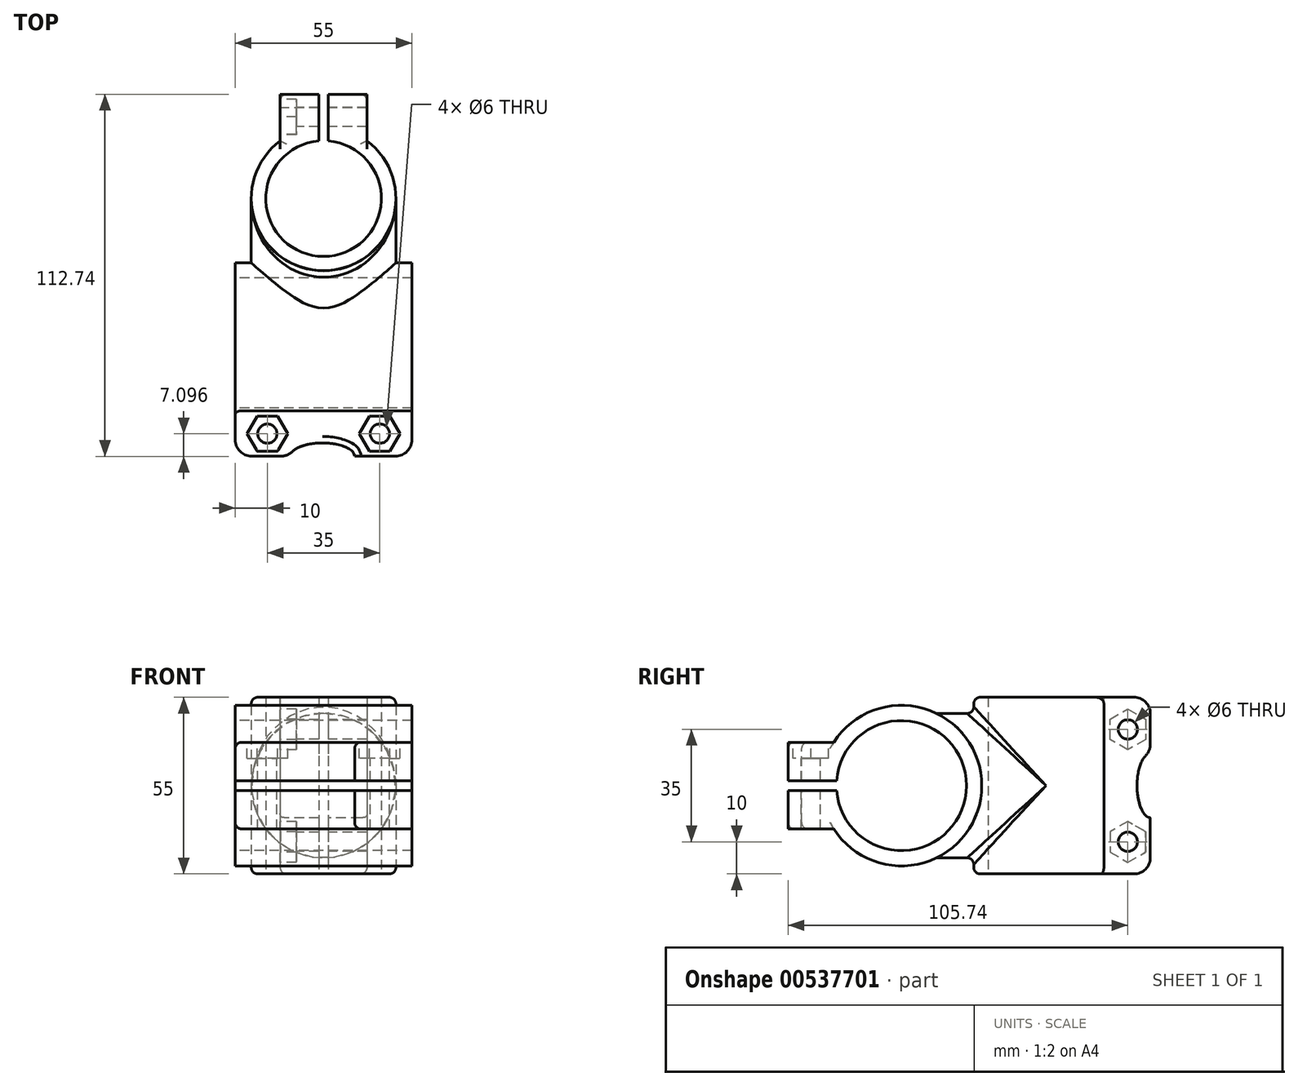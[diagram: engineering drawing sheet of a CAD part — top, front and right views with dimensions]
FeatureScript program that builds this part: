
annotation { "Feature Type Name" : "Feature", "Feature Type Description" : "" }
export const myFeature = defineFeature(function(context is Context, id is Id, definition is map)
    precondition{}
    {
        {
            var Q0;
            Q0=qCreatedBy(makeId("Top.planeOp"),FACE);
            var sketch = newSketch(context, id + "F0", { "sketchPlane" : qUnion([Q0])});
            skArc(sketch, "E0", {"start": v(-1.5, 17.94) * mm, "mid": v(0, -18) * mm, "end": v(1.5, 17.94) * mm});
            skArc(sketch, "E1", {"start": v(-13.5, 18) * mm, "mid": v(0, -22.5) * mm, "end": v(13.5, 18) * mm});
            skLineSegment(sketch, "E2", {"start": v(-1.5, 17.94) * mm, "end": v(-1.5, 22.45) * mm});
            skLineSegment(sketch, "E3", {"start": v(1.5, 17.94) * mm, "end": v(1.5, 22.45) * mm});
            skLineSegment(sketch, "E4", {"start": v(1.5, 20.2) * mm, "end": v(1.5, 22.45) * mm});
            skPoint(sketch, "E4.endSnap0", {"position": v(1.5, 20.2) * mm});
            skLineSegment(sketch, "E5", {"start": v(-1.5, 17.94) * mm, "end": v(-1.5, 32.45) * mm});
            skPoint(sketch, "E5.endSnap0", {"position": v(-1.5, 20.2) * mm});
            skPoint(sketch, "E6.orphan", {"position": v(1.5, 29.76) * mm});
            skLineSegment(sketch, "E7", {"start": v(1.5, 17.94) * mm, "end": v(1.5, 32.45) * mm});
            skLineSegment(sketch, "E8", {"start": v(-13.5, 18) * mm, "end": v(-13.5, 32.45) * mm});
            skLineSegment(sketch, "E9", {"start": v(13.5, 18) * mm, "end": v(13.5, 32.45) * mm});
            skLineSegment(sketch, "E10", {"start": v(-13.5, 32.45) * mm, "end": v(-1.5, 32.45) * mm});
            skLineSegment(sketch, "E11", {"start": v(1.5, 32.45) * mm, "end": v(13.5, 32.45) * mm});
            skSolve(sketch);
        }
        {
            var Q0;
            {var subQ1=sQuery(id+"F0.wireOp",EDGE,"E0");Q0=makeQuery(id+"F0.imprint","IMPRINT",FACE,{"disambiguationData":[TD([[makeQuery(id+"F0.imprint","IMPRINT",EDGE,{"derivedFrom":subQ1}),-1.0]])]});}
            extrude(context, id + "F1", {"entities" : qUnion([Q0]), "depth" : 55 * mm, "offsetDistance" : 25.4 * mm});
        }
        {
            var Q0;
            Q0=qCreatedBy(makeId("Front.planeOp"),FACE);
            var sketch = newSketch(context, id + "F2", { "sketchPlane" : qUnion([Q0])});
            skCircle(sketch, "E12", {"center": v(0, 27.5) * mm, "radius": 22.5 * mm});
            skSolve(sketch);
        }
        {
            var Q0;
            Q0=makeQuery(id+"F2.imprint","IMPRINT",FACE,{"disambiguationData":[TD([[makeQuery(id+"F2.imprint","IMPRINT",EDGE,{"derivedFrom":sQuery(id+"F2.wireOp",EDGE,"E12")}),1.0]])]});
            extrude(context, id + "F3", {"entities" : qUnion([Q0]), "operationType" : NewBodyOperationType.ADD, "depth" : 45 * mm, "offsetDistance" : 25.4 * mm});
        }
        {
            var Q0;
            Q0=makeQuery(id+"F1.opExtrude","CAP_FACE",FACE,{"disambiguationData":[OSD([sQuery(id+"F0.wireOp",EDGE,"E0"),sQuery(id+"F0.wireOp",EDGE,"E1"),sQuery(id+"F0.wireOp",EDGE,"E5"),sQuery(id+"F0.wireOp",EDGE,"E7"),sQuery(id+"F0.wireOp",EDGE,"E8"),sQuery(id+"F0.wireOp",EDGE,"E9"),sQuery(id+"F0.wireOp",EDGE,"E10"),sQuery(id+"F0.wireOp",EDGE,"E11")])],"isStart":true});
            var sketch = newSketch(context, id + "F4", { "sketchPlane" : qUnion([Q0])});
            skPoint(sketch, "E13", {"position": v(0, 0) * mm});
            skCircle(sketch, "E14", {"center": v(0, 0) * mm, "radius": 18 * mm});
            skSolve(sketch);
        }
        {
            var Q0;
            Q0=sQuery(id+"F4.wireOp",VERTEX,"E13");
            var Q1;
            Q1=makeQuery(id+"F1.opExtrude","SWEPT_BODY",BODY,{"disambiguationData":[OSD([sQuery(id+"F0.wireOp",EDGE,"E0"),sQuery(id+"F0.wireOp",EDGE,"E1"),sQuery(id+"F0.wireOp",EDGE,"E5"),sQuery(id+"F0.wireOp",EDGE,"E7"),sQuery(id+"F0.wireOp",EDGE,"E8"),sQuery(id+"F0.wireOp",EDGE,"E9"),sQuery(id+"F0.wireOp",EDGE,"E10"),sQuery(id+"F0.wireOp",EDGE,"E11")])]});
            hole(context, id + "F5", {"style" : HoleStyle.SIMPLE, "endStyle" : HoleEndStyle.THROUGH, "holeDiameter" : 36 * mm, "isTappedThrough" : true, "tappedDepth" : 12.7 * mm, "tapClearance" : 3, "startFromSketch" : true, "locations" : qUnion([Q0]), "scope" : qUnion([Q1])});
        }
        {
            var Q0;
            Q0=qCreatedBy(makeId("Right.planeOp"),FACE);
            var sketch = newSketch(context, id + "F6", { "sketchPlane" : qUnion([Q0])});
            skArc(sketch, "E15", {"start": v(-65.2, 26) * mm, "mid": v(-24.75, 27.5) * mm, "end": v(-65.2, 29) * mm});
            skArc(sketch, "E16", {"start": v(-66.04, 14) * mm, "mid": v(-20, 27.5) * mm, "end": v(-66.04, 41) * mm});
            skLineSegment(sketch, "E17", {"start": v(-45, 27.5) * mm, "end": v(-45.7, 27.5) * mm});
            skLineSegment(sketch, "E18", {"start": v(-65.2, 26) * mm, "end": v(-80.2, 26) * mm});
            skLineSegment(sketch, "E19", {"start": v(-65.2, 29) * mm, "end": v(-80.2, 29) * mm});
            skLineSegment(sketch, "E20", {"start": v(-66.04, 14) * mm, "end": v(-80.2, 14) * mm});
            skLineSegment(sketch, "E21", {"start": v(-80.2, 26) * mm, "end": v(-80.2, 14) * mm});
            skLineSegment(sketch, "E22.MirrorCS", {"start": v(-80.2, 29) * mm, "end": v(-80.2, 41) * mm});
            skLineSegment(sketch, "E23.MirrorCS", {"start": v(-66.04, 41) * mm, "end": v(-80.2, 41) * mm});
            skArc(sketch, "E24.MirrorC", {"start": v(-66.04, 41) * mm, "mid": v(-20, 27.5) * mm, "end": v(-66.04, 14) * mm});
            skArc(sketch, "E25.MirrorC", {"start": v(-65.2, 29) * mm, "mid": v(-24.75, 27.5) * mm, "end": v(-65.2, 26) * mm});
            skPoint(sketch, "E26.orphan", {"position": v(-60.1, 14) * mm});
            skPoint(sketch, "E27.orphan", {"position": v(-60.1, 41) * mm});
            skPoint(sketch, "E28", {"position": v(-45, 68.44) * mm});
            skSolve(sketch);
        }
        {
            var Q0;
            Q0 = qSketchRegion(id + "F6", true);
            extrude(context, id + "F7", {"entities" : qUnion([Q0]), "operationType" : NewBodyOperationType.ADD, "endBound" : BoundingType.SYMMETRIC, "depth" : 55 * mm, "offsetDistance" : 25.4 * mm});
        }
        {
            var Q0;
            Q0=makeQuery(id+"F7.opExtrude","CAP_FACE",FACE,{"disambiguationData":[OSD([sQuery(id+"F6.wireOp",EDGE,"E18"),sQuery(id+"F6.wireOp",EDGE,"E20"),sQuery(id+"F6.wireOp",EDGE,"E21"),sQuery(id+"F6.wireOp",EDGE,"E22.MirrorCS"),sQuery(id+"F6.wireOp",EDGE,"E23.MirrorCS"),sQuery(id+"F6.wireOp",EDGE,"E24.MirrorC"),sQuery(id+"F6.wireOp",EDGE,"E19"),sQuery(id+"F6.wireOp",EDGE,"E25.MirrorC")])],"isStart":false});
            var sketch = newSketch(context, id + "F8", { "sketchPlane" : qUnion([Q0])});
            skPoint(sketch, "E29", {"position": v(-45, 27.5) * mm});
            skSolve(sketch);
        }
        {
            var Q0;
            Q0=sQuery(id+"F8.wireOp",VERTEX,"E29");
            var Q1;
            Q1=makeQuery(id+"F1.opExtrude","SWEPT_BODY",BODY,{"disambiguationData":[OSD([sQuery(id+"F0.wireOp",EDGE,"E0"),sQuery(id+"F0.wireOp",EDGE,"E1"),sQuery(id+"F0.wireOp",EDGE,"E5"),sQuery(id+"F0.wireOp",EDGE,"E7"),sQuery(id+"F0.wireOp",EDGE,"E8"),sQuery(id+"F0.wireOp",EDGE,"E9"),sQuery(id+"F0.wireOp",EDGE,"E10"),sQuery(id+"F0.wireOp",EDGE,"E11")])]});
            hole(context, id + "F9", {"style" : HoleStyle.SIMPLE, "endStyle" : HoleEndStyle.THROUGH, "holeDiameter" : 40.5 * mm, "isTappedThrough" : true, "tappedDepth" : 12.7 * mm, "tapClearance" : 3, "startFromSketch" : true, "locations" : qUnion([Q0]), "scope" : qUnion([Q1])});
        }
        {
            var Q0;
            Q0=makeQuery(id+"F1.opExtrude","SWEPT_FACE",FACE,{"disambiguationData":[OSD([sQuery(id+"F0.wireOp",EDGE,"E8")])]});
            var sketch = newSketch(context, id + "F10", { "sketchPlane" : qUnion([Q0])});
            skCircle(sketch, "E30.cCircle", {"center": v(-25.45, 10) * mm, "radius": 5.5 * mm, "construction": true});
            skLineSegment(sketch, "E30.0", {"start": v(-25.46, 16.35) * mm, "end": v(-19.96, 13.19) * mm});
            skLineSegment(sketch, "E30.1", {"start": v(-19.96, 13.19) * mm, "end": v(-19.94, 6.83) * mm});
            skLineSegment(sketch, "E30.2", {"start": v(-19.94, 6.83) * mm, "end": v(-25.44, 3.65) * mm});
            skLineSegment(sketch, "E30.3", {"start": v(-25.44, 3.65) * mm, "end": v(-30.94, 6.81) * mm});
            skLineSegment(sketch, "E30.4", {"start": v(-30.94, 6.81) * mm, "end": v(-30.96, 13.17) * mm});
            skLineSegment(sketch, "E30.5", {"start": v(-30.96, 13.17) * mm, "end": v(-25.46, 16.35) * mm});
            skPoint(sketch, "E30.0.midPoint", {"position": v(-22.7, 14.77) * mm});
            skPoint(sketch, "E31.endSnap0", {"position": v(-32.45, 27.5) * mm});
            skPoint(sketch, "E31.start.orphan", {"position": v(0, 27.48) * mm});
            skLineSegment(sketch, "E32.MirrorCS", {"start": v(-30.94, 48.19) * mm, "end": v(-30.96, 41.83) * mm});
            skPoint(sketch, "E33.MirrorP", {"position": v(-25.45, 45) * mm});
            skLineSegment(sketch, "E34.MirrorCS", {"start": v(-19.94, 48.17) * mm, "end": v(-25.44, 51.35) * mm});
            skLineSegment(sketch, "E35.MirrorCS", {"start": v(-30.96, 41.83) * mm, "end": v(-25.46, 38.65) * mm});
            skLineSegment(sketch, "E36.MirrorCS", {"start": v(-25.46, 38.65) * mm, "end": v(-19.96, 41.81) * mm});
            skLineSegment(sketch, "E37.MirrorCS", {"start": v(-25.44, 51.35) * mm, "end": v(-30.94, 48.19) * mm});
            skPoint(sketch, "E38.MirrorP", {"position": v(-22.7, 40.23) * mm});
            skLineSegment(sketch, "E39.MirrorCS", {"start": v(-19.96, 41.81) * mm, "end": v(-19.94, 48.17) * mm});
            skCircle(sketch, "E40.MirrorC", {"center": v(-25.45, 45) * mm, "radius": 5.5 * mm, "construction": true});
            skSolve(sketch);
        }
        {
            var Q0;
            Q0 = qSketchRegion(id + "F10", true);
            extrude(context, id + "F11", {"entities" : qUnion([Q0]), "operationType" : NewBodyOperationType.REMOVE, "oppositeDirection" : true, "depth" : 5 * mm, "offsetDistance" : 25.4 * mm});
        }
        {
            var Q0;
            Q0=makeQuery(id+"F1.opExtrude","SWEPT_FACE",FACE,{"disambiguationData":[OSD([sQuery(id+"F0.wireOp",EDGE,"E8")])]});
            var sketch = newSketch(context, id + "F12", { "sketchPlane" : qUnion([Q0])});
            skPoint(sketch, "E41", {"position": v(-25.45, 10) * mm});
            skPoint(sketch, "E42.orphan", {"position": v(-19.96, 13.19) * mm});
            skPoint(sketch, "E43.start.orphan", {"position": v(-30.94, 6.81) * mm});
            skPoint(sketch, "E44.start.orphan", {"position": v(0, 27.52) * mm});
            skLineSegment(sketch, "E45", {"start": v(-38, 27.98) * mm, "end": v(-12.83, 27.98) * mm});
            skSolve(sketch);
        }
        {
            var Q0;
            Q0=sQuery(id+"F12.wireOp",VERTEX,"f4a95eb3-fcfc-4df5-b017-d8c500dd858f2.MirrorP");
            var Q1;
            Q1=sQuery(id+"F12.wireOp",VERTEX,"E41");
            var Q2;
            Q2=makeQuery(id+"F1.opExtrude","SWEPT_BODY",BODY,{"disambiguationData":[OSD([sQuery(id+"F0.wireOp",EDGE,"E0"),sQuery(id+"F0.wireOp",EDGE,"E1"),sQuery(id+"F0.wireOp",EDGE,"E5"),sQuery(id+"F0.wireOp",EDGE,"E7"),sQuery(id+"F0.wireOp",EDGE,"E8"),sQuery(id+"F0.wireOp",EDGE,"E9"),sQuery(id+"F0.wireOp",EDGE,"E10"),sQuery(id+"F0.wireOp",EDGE,"E11")])]});
            hole(context, id + "F13", {"style" : HoleStyle.SIMPLE, "endStyle" : HoleEndStyle.THROUGH, "holeDiameter" : 6 * mm, "isTappedThrough" : true, "tappedDepth" : 12.7 * mm, "tapClearance" : 3, "startFromSketch" : true, "locations" : qUnion([Q0, Q1]), "scope" : qUnion([Q2])});
        }
        {
            var Q0;
            Q0=makeQuery(id+"F7.opExtrude","SWEPT_FACE",FACE,{"disambiguationData":[OSD([sQuery(id+"F6.wireOp",EDGE,"E23.MirrorCS")])]});
            var sketch = newSketch(context, id + "F14", { "sketchPlane" : qUnion([Q0])});
            skCircle(sketch, "E46.cCircle", {"center": v(-17.5, -73.2) * mm, "radius": 5.5 * mm, "construction": true});
            skLineSegment(sketch, "E46.0", {"start": v(-11.15, -73.2) * mm, "end": v(-14.32, -78.7) * mm});
            skLineSegment(sketch, "E46.1", {"start": v(-14.32, -78.7) * mm, "end": v(-20.68, -78.7) * mm});
            skLineSegment(sketch, "E46.2", {"start": v(-20.68, -78.7) * mm, "end": v(-23.85, -73.2) * mm});
            skLineSegment(sketch, "E46.3", {"start": v(-23.85, -73.2) * mm, "end": v(-20.68, -67.7) * mm});
            skLineSegment(sketch, "E46.4", {"start": v(-20.68, -67.7) * mm, "end": v(-14.32, -67.7) * mm});
            skLineSegment(sketch, "E46.5", {"start": v(-14.32, -67.7) * mm, "end": v(-11.15, -73.2) * mm});
            skPoint(sketch, "E46.0.midPoint", {"position": v(-12.74, -75.94) * mm});
            skLineSegment(sketch, "E47.MirrorCS", {"start": v(11.15, -73.2) * mm, "end": v(14.32, -78.7) * mm});
            skCircle(sketch, "E48.MirrorC", {"center": v(17.5, -73.2) * mm, "radius": 5.5 * mm, "construction": true});
            skPoint(sketch, "E49.MirrorP", {"position": v(12.74, -75.94) * mm});
            skLineSegment(sketch, "E50.MirrorCS", {"start": v(14.32, -78.7) * mm, "end": v(20.68, -78.7) * mm});
            skLineSegment(sketch, "E51.MirrorCS", {"start": v(20.68, -67.7) * mm, "end": v(14.32, -67.7) * mm});
            skLineSegment(sketch, "E52.MirrorCS", {"start": v(14.32, -67.7) * mm, "end": v(11.15, -73.2) * mm});
            skLineSegment(sketch, "E53.MirrorCS", {"start": v(23.85, -73.2) * mm, "end": v(20.68, -67.7) * mm});
            skLineSegment(sketch, "E54.MirrorCS", {"start": v(20.68, -78.7) * mm, "end": v(23.85, -73.2) * mm});
            skSolve(sketch);
        }
        {
            var Q0;
            Q0=sQuery(id+"F14.wireOp",VERTEX,"E46.cCircle.center");
            var Q1;
            Q1=sQuery(id+"F14.wireOp",VERTEX,"E48.MirrorC.center");
            var Q2;
            Q2=makeQuery(id+"F1.opExtrude","SWEPT_BODY",BODY,{"disambiguationData":[OSD([sQuery(id+"F0.wireOp",EDGE,"E0"),sQuery(id+"F0.wireOp",EDGE,"E1"),sQuery(id+"F0.wireOp",EDGE,"E5"),sQuery(id+"F0.wireOp",EDGE,"E7"),sQuery(id+"F0.wireOp",EDGE,"E8"),sQuery(id+"F0.wireOp",EDGE,"E9"),sQuery(id+"F0.wireOp",EDGE,"E10"),sQuery(id+"F0.wireOp",EDGE,"E11")])]});
            hole(context, id + "F15", {"style" : HoleStyle.SIMPLE, "endStyle" : HoleEndStyle.THROUGH, "holeDiameter" : 6 * mm, "isTappedThrough" : true, "tappedDepth" : 12.7 * mm, "tapClearance" : 3, "startFromSketch" : true, "locations" : qUnion([Q0, Q1]), "scope" : qUnion([Q2])});
        }
        {
            var Q0;
            Q0 = qSketchRegion(id + "F14", true);
            extrude(context, id + "F16", {"entities" : qUnion([Q0]), "operationType" : NewBodyOperationType.REMOVE, "oppositeDirection" : true, "depth" : 5 * mm, "offsetDistance" : 25.4 * mm});
        }
        {
            var Q0;
            Q0=makeQuery(id+"F7.opExtrude","CAP_EDGE",EDGE,{"disambiguationData":[OSD([sQuery(id+"F6.wireOp",EDGE,"E22.MirrorCS")])],"isStart":true});
            var Q1;
            Q1=makeQuery(id+"F7.opExtrude","CAP_EDGE",EDGE,{"disambiguationData":[OSD([sQuery(id+"F6.wireOp",EDGE,"E21")])],"isStart":true});
            var Q2;
            Q2=makeQuery(id+"F7.opExtrude","CAP_EDGE",EDGE,{"disambiguationData":[OSD([sQuery(id+"F6.wireOp",EDGE,"E22.MirrorCS")])],"isStart":false});
            var Q3;
            Q3=makeQuery(id+"F7.opExtrude","CAP_EDGE",EDGE,{"disambiguationData":[OSD([sQuery(id+"F6.wireOp",EDGE,"E21")])],"isStart":false});
            var Q4;
            Q4=makeQuery(id+"F1.opExtrude","CAP_EDGE",EDGE,{"disambiguationData":[OSD([sQuery(id+"F0.wireOp",EDGE,"E10")])],"isStart":false});
            var Q5;
            Q5=makeQuery(id+"F1.opExtrude","CAP_EDGE",EDGE,{"disambiguationData":[OSD([sQuery(id+"F0.wireOp",EDGE,"E11")])],"isStart":false});
            var Q6;
            Q6=makeQuery(id+"F1.opExtrude","CAP_EDGE",EDGE,{"disambiguationData":[OSD([sQuery(id+"F0.wireOp",EDGE,"E11")])],"isStart":true});
            var Q7;
            Q7=makeQuery(id+"F1.opExtrude","CAP_EDGE",EDGE,{"disambiguationData":[OSD([sQuery(id+"F0.wireOp",EDGE,"E10")])],"isStart":true});
            fillet(context, id + "F17", {"entities" : qUnion([Q0, Q1, Q2, Q3, Q4, Q5, Q6, Q7]), "radius" : 5.08 * mm, "tangentPropagation" : true, "allowEdgeOverflow" : false});
        }
        {
            var Q0;
            Q0=makeQuery(id+"F1.opExtrude","SWEPT_FACE",FACE,{"disambiguationData":[OSD([sQuery(id+"F0.wireOp",EDGE,"E8")])]});
            var sketch = newSketch(context, id + "F18", { "sketchPlane" : qUnion([Q0])});
            skLineSegment(sketch, "E55", {"start": v(0, 27.5) * mm, "end": v(-38.35, 27.5) * mm});
            skLineSegment(sketch, "E56", {"start": v(-32.45, 37.5) * mm, "end": v(-32.45, 27.5) * mm});
            skLineSegment(sketch, "E57", {"start": v(-32.45, 27.5) * mm, "end": v(-32.45, 17.5) * mm});
            skFitSpline(sketch, "E58", {"points": [v(-32.45, 37.5) * mm, v(-28.32, 27.5) * mm, v(-32.45, 17.5) * mm, v(-38.35, 27.5) * mm, v(-32.45, 37.5) * mm]});
            skSolve(sketch);
        }
        {
            var Q0;
            Q0 = qSketchRegion(id + "F18", true);
            extrude(context, id + "F19", {"entities" : qUnion([Q0]), "operationType" : NewBodyOperationType.REMOVE, "oppositeDirection" : true, "depth" : 50.8 * mm, "offsetDistance" : 25.4 * mm});
        }
        {
            var Q0;
            Q0=makeQuery(id+"F19.boolean.opBoolean","INTERSECT",EDGE,{"disambiguationData":[OD(1.0)],"derivedFrom":[makeQuery(id+"F1.opExtrude","SWEPT_FACE",FACE,{"disambiguationData":[OSD([sQuery(id+"F0.wireOp",EDGE,"E10")])]}),makeQuery(id+"F19.opExtrude","SWEPT_FACE",FACE,{"disambiguationData":[OSD([sQuery(id+"F18.wireOp",EDGE,"E58")])]})]});
            var Q1;
            Q1=makeQuery(id+"F19.boolean.opBoolean","INTERSECT",EDGE,{"disambiguationData":[OD(1.0)],"derivedFrom":[makeQuery(id+"F1.opExtrude","SWEPT_FACE",FACE,{"disambiguationData":[OSD([sQuery(id+"F0.wireOp",EDGE,"E11")])]}),makeQuery(id+"F19.opExtrude","SWEPT_FACE",FACE,{"disambiguationData":[OSD([sQuery(id+"F18.wireOp",EDGE,"E58")])]})]});
            var Q2;
            Q2=makeQuery(id+"F19.boolean.opBoolean","INTERSECT",EDGE,{"disambiguationData":[OD(0.0)],"derivedFrom":[makeQuery(id+"F1.opExtrude","SWEPT_FACE",FACE,{"disambiguationData":[OSD([sQuery(id+"F0.wireOp",EDGE,"E11")])]}),makeQuery(id+"F19.opExtrude","SWEPT_FACE",FACE,{"disambiguationData":[OSD([sQuery(id+"F18.wireOp",EDGE,"E58")])]})]});
            var Q3;
            Q3=makeQuery(id+"F19.boolean.opBoolean","INTERSECT",EDGE,{"disambiguationData":[OD(0.0)],"derivedFrom":[makeQuery(id+"F1.opExtrude","SWEPT_FACE",FACE,{"disambiguationData":[OSD([sQuery(id+"F0.wireOp",EDGE,"E10")])]}),makeQuery(id+"F19.opExtrude","SWEPT_FACE",FACE,{"disambiguationData":[OSD([sQuery(id+"F18.wireOp",EDGE,"E58")])]})]});
            fillet(context, id + "F20", {"entities" : qUnion([Q0, Q1, Q2, Q3]), "radius" : 5.08 * mm, "tangentPropagation" : true, "allowEdgeOverflow" : false});
        }
        {
            var Q0;
            Q0=makeQuery(id+"F7.opExtrude","SWEPT_FACE",FACE,{"disambiguationData":[OSD([sQuery(id+"F6.wireOp",EDGE,"E23.MirrorCS")])]});
            var sketch = newSketch(context, id + "F21", { "sketchPlane" : qUnion([Q0])});
            skLineSegment(sketch, "E59", {"start": v(-0.35, -47.74) * mm, "end": v(-0.35, -86.09) * mm});
            skLineSegment(sketch, "E60", {"start": v(-10.35, -80.2) * mm, "end": v(-0.35, -80.2) * mm});
            skLineSegment(sketch, "E61", {"start": v(-0.35, -80.2) * mm, "end": v(9.65, -80.2) * mm});
            skFitSpline(sketch, "E62", {"points": [v(-10.35, -80.2) * mm, v(-0.35, -76.07) * mm, v(9.65, -80.2) * mm, v(-0.35, -86.09) * mm, v(-10.35, -80.2) * mm]});
            skSolve(sketch);
        }
        {
            var Q0;
            Q0 = qSketchRegion(id + "F21", true);
            extrude(context, id + "F22", {"entities" : qUnion([Q0]), "operationType" : NewBodyOperationType.REMOVE, "oppositeDirection" : true, "depth" : 50.8 * mm, "offsetDistance" : 25.4 * mm});
        }
        {
            var Q0;
            Q0=makeQuery(id+"F22.boolean.opBoolean","INTERSECT",EDGE,{"disambiguationData":[OD(0.0)],"derivedFrom":[makeQuery(id+"F7.opExtrude","SWEPT_FACE",FACE,{"disambiguationData":[OSD([sQuery(id+"F6.wireOp",EDGE,"E22.MirrorCS")])]}),makeQuery(id+"F22.opExtrude","SWEPT_FACE",FACE,{"disambiguationData":[OSD([sQuery(id+"F21.wireOp",EDGE,"E62")])]})]});
            var Q1;
            Q1=makeQuery(id+"F22.boolean.opBoolean","INTERSECT",EDGE,{"disambiguationData":[OD(0.0)],"derivedFrom":[makeQuery(id+"F7.opExtrude","SWEPT_FACE",FACE,{"disambiguationData":[OSD([sQuery(id+"F6.wireOp",EDGE,"E21")])]}),makeQuery(id+"F22.opExtrude","SWEPT_FACE",FACE,{"disambiguationData":[OSD([sQuery(id+"F21.wireOp",EDGE,"E62")])]})]});
            var Q2;
            Q2=makeQuery(id+"F22.boolean.opBoolean","INTERSECT",EDGE,{"disambiguationData":[OD(1.0)],"derivedFrom":[makeQuery(id+"F7.opExtrude","SWEPT_FACE",FACE,{"disambiguationData":[OSD([sQuery(id+"F6.wireOp",EDGE,"E22.MirrorCS")])]}),makeQuery(id+"F22.opExtrude","SWEPT_FACE",FACE,{"disambiguationData":[OSD([sQuery(id+"F21.wireOp",EDGE,"E62")])]})]});
            var Q3;
            Q3=makeQuery(id+"F22.boolean.opBoolean","INTERSECT",EDGE,{"disambiguationData":[OD(1.0)],"derivedFrom":[makeQuery(id+"F7.opExtrude","SWEPT_FACE",FACE,{"disambiguationData":[OSD([sQuery(id+"F6.wireOp",EDGE,"E21")])]}),makeQuery(id+"F22.opExtrude","SWEPT_FACE",FACE,{"disambiguationData":[OSD([sQuery(id+"F21.wireOp",EDGE,"E62")])]})]});
            fillet(context, id + "F23", {"entities" : qUnion([Q0, Q1, Q2, Q3]), "radius" : 5.08 * mm, "tangentPropagation" : true, "allowEdgeOverflow" : false});
        }
        {
            var Q0;
            Q0=sQuery(id+"F10.wireOp",VERTEX,"E33.MirrorP");
            var Q1;
            Q1=makeQuery(id+"F1.opExtrude","SWEPT_BODY",BODY,{"disambiguationData":[OSD([sQuery(id+"F0.wireOp",EDGE,"E0"),sQuery(id+"F0.wireOp",EDGE,"E1"),sQuery(id+"F0.wireOp",EDGE,"E5"),sQuery(id+"F0.wireOp",EDGE,"E7"),sQuery(id+"F0.wireOp",EDGE,"E8"),sQuery(id+"F0.wireOp",EDGE,"E9"),sQuery(id+"F0.wireOp",EDGE,"E10"),sQuery(id+"F0.wireOp",EDGE,"E11")])]});
            hole(context, id + "F24", {"style" : HoleStyle.SIMPLE, "endStyle" : HoleEndStyle.THROUGH, "holeDiameter" : 6 * mm, "isTappedThrough" : true, "tappedDepth" : 12.7 * mm, "tapClearance" : 3, "startFromSketch" : true, "locations" : qUnion([Q0]), "scope" : qUnion([Q1])});
        }
        {
            var Q0;
            Q0=makeQuery(id+"F1.opExtrude","CAP_EDGE",EDGE,{"disambiguationData":[OSD([sQuery(id+"F0.wireOp",EDGE,"E1")])],"isStart":false});
            var Q1;
            Q1=makeQuery(id+"F7.opExtrude","CAP_EDGE",EDGE,{"disambiguationData":[OSD([sQuery(id+"F6.wireOp",EDGE,"E24.MirrorC")])],"isStart":true});
            var Q2;
            Q2=makeQuery(id+"F7.opExtrude","CAP_EDGE",EDGE,{"disambiguationData":[OSD([sQuery(id+"F6.wireOp",EDGE,"E24.MirrorC")])],"isStart":false});
            var Q3;
            Q3=makeQuery(id+"F1.opExtrude","CAP_EDGE",EDGE,{"disambiguationData":[OSD([sQuery(id+"F0.wireOp",EDGE,"E1")])],"isStart":true});
            var Q4;
            Q4=makeQuery(id+"F7.opExtrude","CAP_EDGE",EDGE,{"disambiguationData":[OSD([sQuery(id+"F6.wireOp",EDGE,"E20")])],"isStart":true});
            var Q5;
            Q5=makeQuery(id+"F7.opExtrude","CAP_EDGE",EDGE,{"disambiguationData":[OSD([sQuery(id+"F6.wireOp",EDGE,"E23.MirrorCS")])],"isStart":true});
            var Q6;
            Q6=makeQuery(id+"F1.opExtrude","CAP_EDGE",EDGE,{"disambiguationData":[OSD([sQuery(id+"F0.wireOp",EDGE,"E8")])],"isStart":true});
            var Q7;
            Q7=makeQuery(id+"F1.opExtrude","CAP_EDGE",EDGE,{"disambiguationData":[OSD([sQuery(id+"F0.wireOp",EDGE,"E9")])],"isStart":true});
            fillet(context, id + "F25", {"entities" : qUnion([Q0, Q1, Q2, Q3, Q4, Q5, Q6, Q7]), "radius" : 2 * mm, "tangentPropagation" : true, "allowEdgeOverflow" : false});
        }
        {
            var Q0;
            Q0=makeQuery(id+"F3.boolean.opBoolean","INTERSECT",EDGE,{"disambiguationData":[OD(1.0)],"derivedFrom":[makeQuery(id+"F1.opExtrude","SWEPT_FACE",FACE,{"disambiguationData":[OSD([sQuery(id+"F0.wireOp",EDGE,"E1")])]}),makeQuery(id+"F3.opExtrude","SWEPT_FACE",FACE,{"disambiguationData":[OSD([sQuery(id+"F2.wireOp",EDGE,"E12")])]})]});
            var Q1;
            Q1=makeQuery(id+"F3.boolean.opBoolean","INTERSECT",EDGE,{"disambiguationData":[OD(0.0)],"derivedFrom":[makeQuery(id+"F1.opExtrude","SWEPT_FACE",FACE,{"disambiguationData":[OSD([sQuery(id+"F0.wireOp",EDGE,"E1")])]}),makeQuery(id+"F3.opExtrude","SWEPT_FACE",FACE,{"disambiguationData":[OSD([sQuery(id+"F2.wireOp",EDGE,"E12")])]})]});
            var Q2;
            {var subQ0=sQuery(id+"F2.wireOp",EDGE,"E12");Q2=makeQuery(id+"F7.boolean.opBoolean","INTERSECT",EDGE,{"derivedFrom":[makeQuery(id+"F3.boolean.opBoolean","SPLIT",FACE,{"disambiguationData":[TD([makeQuery(id+"F1.opExtrude","SWEPT_FACE",FACE,{"disambiguationData":[OSD([sQuery(id+"F0.wireOp",EDGE,"E1")])]}),makeQuery(id+"F3.opExtrude","CAP_FACE",FACE,{"disambiguationData":[OSD([subQ0])],"isStart":false})])],"derivedFrom":makeQuery(id+"F3.opExtrude","SWEPT_FACE",FACE,{"disambiguationData":[OSD([subQ0])]})}),makeQuery(id+"F7.opExtrude","SWEPT_FACE",FACE,{"disambiguationData":[OSD([sQuery(id+"F6.wireOp",EDGE,"E24.MirrorC")])]})]});}
            fillet(context, id + "F26", {"entities" : qUnion([Q0, Q1, Q2]), "radius" : 2 * mm, "tangentPropagation" : true, "allowEdgeOverflow" : false});
        }
    });
